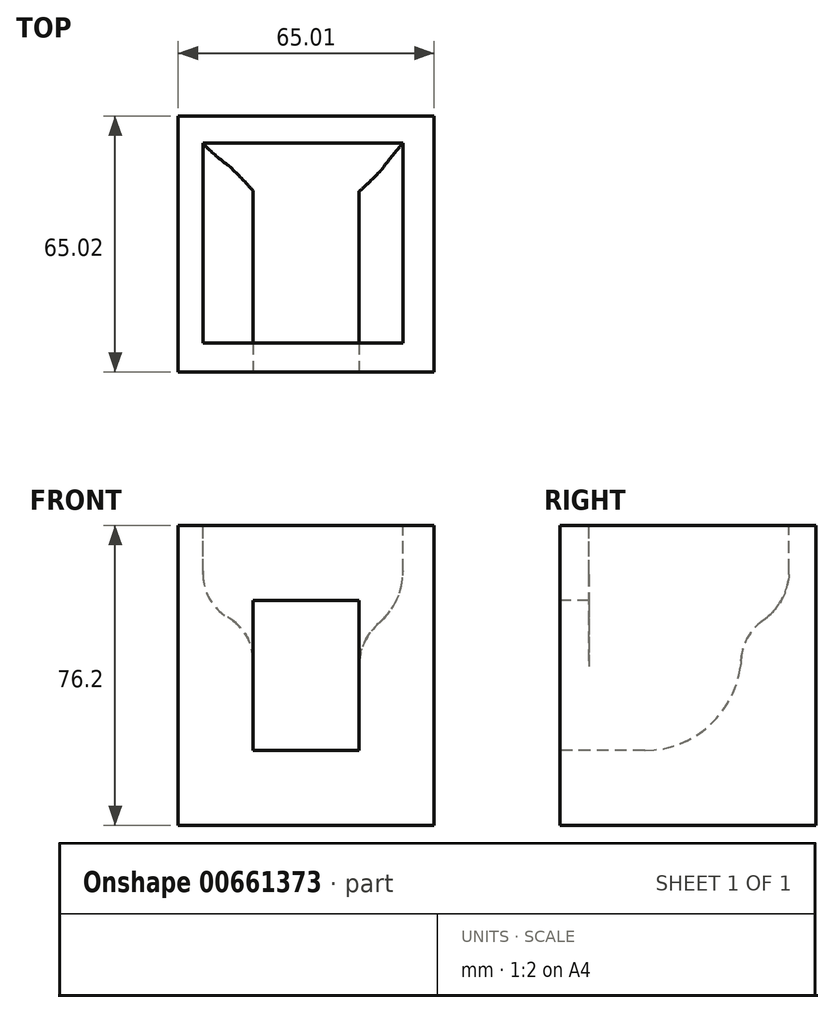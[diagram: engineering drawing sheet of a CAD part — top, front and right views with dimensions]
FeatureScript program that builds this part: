
annotation { "Feature Type Name" : "Feature", "Feature Type Description" : "" }
export const myFeature = defineFeature(function(context is Context, id is Id, definition is map)
    precondition{}
    {
        {
            var Q0;
            Q0=qCreatedBy(makeId("Top.planeOp"),FACE);
            var sketch = newSketch(context, id + "F0", { "sketchPlane" : qUnion([Q0])});
            skLineSegment(sketch, "E0.bottom", {"start": v(-28.8, 28.66) * mm, "end": v(36.22, 28.66) * mm});
            skLineSegment(sketch, "E0.top", {"start": v(-28.8, -36.36) * mm, "end": v(36.22, -36.36) * mm});
            skLineSegment(sketch, "E0.left", {"start": v(-28.8, 28.66) * mm, "end": v(-28.8, -36.36) * mm});
            skLineSegment(sketch, "E0.right", {"start": v(36.22, 28.66) * mm, "end": v(36.22, -36.36) * mm});
            skSolve(sketch);
        }
        {
            var Q0;
            Q0=makeQuery(id+"F0.imprint","IMPRINT",FACE,{"disambiguationData":[TD([[makeQuery(id+"F0.imprint","IMPRINT",EDGE,{"derivedFrom":sQuery(id+"F0.wireOp",EDGE,"E0.bottom")}),-1.0]])]});
            extrude(context, id + "F1", {"entities" : qUnion([Q0]), "depth" : 76.2 * mm, "offsetDistance" : 25.4 * mm});
        }
        {
            var Q0;
            Q0=makeQuery(id+"F1.opExtrude","SWEPT_FACE",FACE,{"disambiguationData":[OSD([sQuery(id+"F0.wireOp",EDGE,"E0.top")])]});
            shell(context, id + "F2", {"entities" : qUnion([Q0]), "thickness" : 19.05 * mm});
        }
        {
            var Q0;
            Q0=makeQuery(id+"F1.opExtrude","CAP_FACE",FACE,{"disambiguationData":[OSD([sQuery(id+"F0.wireOp",EDGE,"E0.bottom"),sQuery(id+"F0.wireOp",EDGE,"E0.top"),sQuery(id+"F0.wireOp",EDGE,"E0.left"),sQuery(id+"F0.wireOp",EDGE,"E0.right")])],"isStart":false});
            var sketch = newSketch(context, id + "F3", { "sketchPlane" : qUnion([Q0])});
            skLineSegment(sketch, "E1.bottom", {"start": v(-22.48, 21.82) * mm, "end": v(28.32, 21.82) * mm});
            skLineSegment(sketch, "E1.top", {"start": v(-22.48, -28.98) * mm, "end": v(28.32, -28.98) * mm});
            skLineSegment(sketch, "E1.left", {"start": v(-22.48, 21.82) * mm, "end": v(-22.48, -28.98) * mm});
            skLineSegment(sketch, "E1.right", {"start": v(28.32, 21.82) * mm, "end": v(28.32, -28.98) * mm});
            skSolve(sketch);
        }
        {
            var Q0;
            Q0 = qSketchRegion(id + "F3", true);
            extrude(context, id + "F4", {"entities" : qUnion([Q0]), "operationType" : NewBodyOperationType.REMOVE, "oppositeDirection" : true, "depth" : 21.59 * mm, "offsetDistance" : 25.4 * mm});
        }
        {
            var Q0;
            Q0=makeQuery(id+"F4.boolean.opBoolean","INTERSECT",EDGE,{"derivedFrom":[makeQuery(id+"F2.opShell","OFFSET_FACE",FACE,{"disambiguationData":[OSD([sQuery(id+"F0.wireOp",EDGE,"E0.bottom")])]}),makeQuery(id+"F4.opExtrude","CAP_FACE",FACE,{"disambiguationData":[OSD([sQuery(id+"F3.wireOp",EDGE,"E1.bottom"),sQuery(id+"F3.wireOp",EDGE,"E1.top"),sQuery(id+"F3.wireOp",EDGE,"E1.left"),sQuery(id+"F3.wireOp",EDGE,"E1.right")])],"isStart":false})]});
            fillet(context, id + "F5", {"entities" : qUnion([Q0]), "radius" : 13.5 * mm, "tangentPropagation" : true, "allowEdgeOverflow" : false});
        }
        {
            var Q0;
            Q0=makeQuery(id+"F4.boolean.opBoolean","INTERSECT",EDGE,{"derivedFrom":[makeQuery(id+"F2.opShell","OFFSET_FACE",FACE,{"disambiguationData":[OSD([sQuery(id+"F0.wireOp",EDGE,"E0.left")])]}),makeQuery(id+"F4.opExtrude","CAP_FACE",FACE,{"disambiguationData":[OSD([sQuery(id+"F3.wireOp",EDGE,"E1.bottom"),sQuery(id+"F3.wireOp",EDGE,"E1.top"),sQuery(id+"F3.wireOp",EDGE,"E1.left"),sQuery(id+"F3.wireOp",EDGE,"E1.right")])],"isStart":false})]});
            fillet(context, id + "F6", {"entities" : qUnion([Q0]), "radius" : 12.88 * mm, "tangentPropagation" : true, "allowEdgeOverflow" : false});
        }
        {
            var Q0;
            Q0=makeQuery(id+"F4.boolean.opBoolean","INTERSECT",EDGE,{"derivedFrom":[makeQuery(id+"F2.opShell","OFFSET_FACE",FACE,{"disambiguationData":[OSD([sQuery(id+"F0.wireOp",EDGE,"E0.right")])]}),makeQuery(id+"F4.opExtrude","CAP_FACE",FACE,{"disambiguationData":[OSD([sQuery(id+"F3.wireOp",EDGE,"E1.bottom"),sQuery(id+"F3.wireOp",EDGE,"E1.top"),sQuery(id+"F3.wireOp",EDGE,"E1.left"),sQuery(id+"F3.wireOp",EDGE,"E1.right")])],"isStart":false})]});
            fillet(context, id + "F7", {"entities" : qUnion([Q0]), "radius" : 14.72 * mm, "tangentPropagation" : true, "allowEdgeOverflow" : false});
        }
        {
            var Q0;
            {var subQ0=sQuery(id+"F0.wireOp",EDGE,"E0.bottom");Q0=makeQuery(id+"F2.opShell","OFFSET_EDGE",EDGE,{"disambiguationData":[OSD([subQ0]),TDD([makeQuery(id+"F1.opExtrude","CAP_EDGE",EDGE,{"disambiguationData":[OSD([subQ0])],"isStart":true})])]});}
            fillet(context, id + "F8", {"entities" : qUnion([Q0]), "radius" : 24.53 * mm, "tangentPropagation" : true, "allowEdgeOverflow" : false});
        }
        {
            var Q0;
            {var subQ0=sQuery(id+"F3.wireOp",EDGE,"E1.bottom");Q0=makeQuery(id+"F5.opFillet","BLEND_EDGE",EDGE,{"blendedFrom":[makeQuery(id+"F4.boolean.opBoolean","INTERSECT",EDGE,{"derivedFrom":[makeQuery(id+"F2.opShell","OFFSET_FACE",FACE,{"disambiguationData":[OSD([sQuery(id+"F0.wireOp",EDGE,"E0.bottom")])]}),makeQuery(id+"F4.opExtrude","CAP_FACE",FACE,{"disambiguationData":[OSD([subQ0,sQuery(id+"F3.wireOp",EDGE,"E1.top"),sQuery(id+"F3.wireOp",EDGE,"E1.left"),sQuery(id+"F3.wireOp",EDGE,"E1.right")])],"isStart":false})]}),makeQuery(id+"F4.boolean.opBoolean","COPY",FACE,{"derivedFrom":makeQuery(id+"F4.opExtrude","SWEPT_FACE",FACE,{"disambiguationData":[OSD([subQ0])]})})],"blendedInto":[makeQuery(id+"F4.boolean.opBoolean","COPY",FACE,{"derivedFrom":makeQuery(id+"F4.opExtrude","SWEPT_FACE",FACE,{"disambiguationData":[OSD([subQ0])]})})]});}
            fillet(context, id + "F9", {"entities" : qUnion([Q0]), "radius" : 15.17 * mm, "tangentPropagation" : true, "allowEdgeOverflow" : false});
        }
        {
            var Q0;
            {var subQ0=sQuery(id+"F3.wireOp",EDGE,"E1.left");Q0=makeQuery(id+"F6.opFillet","BLEND_EDGE",EDGE,{"blendedFrom":[makeQuery(id+"F4.boolean.opBoolean","INTERSECT",EDGE,{"derivedFrom":[makeQuery(id+"F2.opShell","OFFSET_FACE",FACE,{"disambiguationData":[OSD([sQuery(id+"F0.wireOp",EDGE,"E0.left")])]}),makeQuery(id+"F4.opExtrude","CAP_FACE",FACE,{"disambiguationData":[OSD([sQuery(id+"F3.wireOp",EDGE,"E1.bottom"),sQuery(id+"F3.wireOp",EDGE,"E1.top"),subQ0,sQuery(id+"F3.wireOp",EDGE,"E1.right")])],"isStart":false})]}),makeQuery(id+"F4.boolean.opBoolean","COPY",FACE,{"derivedFrom":makeQuery(id+"F4.opExtrude","SWEPT_FACE",FACE,{"disambiguationData":[OSD([subQ0])]})})],"blendedInto":[makeQuery(id+"F4.boolean.opBoolean","COPY",FACE,{"derivedFrom":makeQuery(id+"F4.opExtrude","SWEPT_FACE",FACE,{"disambiguationData":[OSD([subQ0])]})})]});}
            fillet(context, id + "F10", {"entities" : qUnion([Q0]), "radius" : 12.5 * mm, "tangentPropagation" : true, "allowEdgeOverflow" : false});
        }
        {
            var Q0;
            {var subQ0=sQuery(id+"F3.wireOp",EDGE,"E1.right");Q0=makeQuery(id+"F7.opFillet","BLEND_EDGE",EDGE,{"blendedFrom":[makeQuery(id+"F4.boolean.opBoolean","INTERSECT",EDGE,{"derivedFrom":[makeQuery(id+"F2.opShell","OFFSET_FACE",FACE,{"disambiguationData":[OSD([sQuery(id+"F0.wireOp",EDGE,"E0.right")])]}),makeQuery(id+"F4.opExtrude","CAP_FACE",FACE,{"disambiguationData":[OSD([sQuery(id+"F3.wireOp",EDGE,"E1.bottom"),sQuery(id+"F3.wireOp",EDGE,"E1.top"),sQuery(id+"F3.wireOp",EDGE,"E1.left"),subQ0])],"isStart":false})]}),makeQuery(id+"F4.boolean.opBoolean","COPY",FACE,{"derivedFrom":makeQuery(id+"F4.opExtrude","SWEPT_FACE",FACE,{"disambiguationData":[OSD([subQ0])]})})],"blendedInto":[makeQuery(id+"F4.boolean.opBoolean","COPY",FACE,{"derivedFrom":makeQuery(id+"F4.opExtrude","SWEPT_FACE",FACE,{"disambiguationData":[OSD([subQ0])]})})]});}
            fillet(context, id + "F11", {"entities" : qUnion([Q0]), "radius" : 17.02 * mm, "tangentPropagation" : true, "allowEdgeOverflow" : false});
        }
    });
